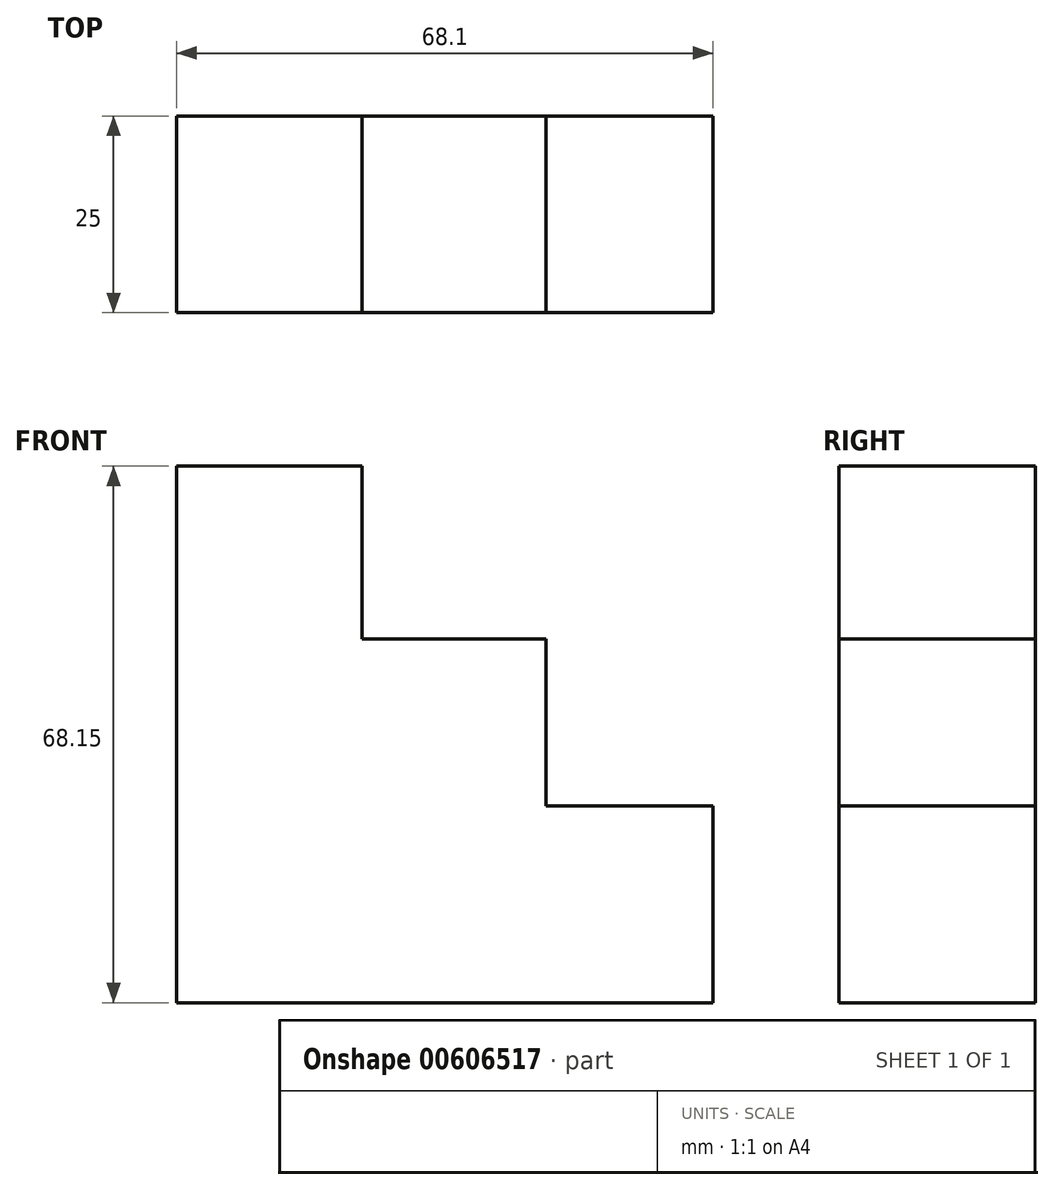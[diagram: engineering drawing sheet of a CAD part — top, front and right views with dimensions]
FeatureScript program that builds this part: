
annotation { "Feature Type Name" : "Feature", "Feature Type Description" : "" }
export const myFeature = defineFeature(function(context is Context, id is Id, definition is map)
    precondition{}
    {
        {
            var Q0;
            Q0=qCreatedBy(makeId("Front.planeOp"),FACE);
            var sketch = newSketch(context, id + "F0", { "sketchPlane" : qUnion([Q0])});
            skLineSegment(sketch, "E0", {"start": v(-51.9, 32.73) * mm, "end": v(-51.9, -35.42) * mm});
            skLineSegment(sketch, "E1", {"start": v(-51.9, -35.42) * mm, "end": v(16.2, -35.42) * mm});
            skLineSegment(sketch, "E2", {"start": v(16.2, -35.42) * mm, "end": v(16.2, -10.42) * mm});
            skLineSegment(sketch, "E3", {"start": v(16.2, -10.42) * mm, "end": v(-4.95, -10.42) * mm});
            skLineSegment(sketch, "E4", {"start": v(-51.9, 32.73) * mm, "end": v(-28.35, 32.73) * mm});
            skLineSegment(sketch, "E5", {"start": v(-4.95, -10.42) * mm, "end": v(-4.95, 10.2) * mm});
            skLineSegment(sketch, "E6", {"start": v(-28.35, 32.73) * mm, "end": v(-28.35, 10.8) * mm});
            skLineSegment(sketch, "E7", {"start": v(-28.35, 10.8) * mm, "end": v(-4.95, 10.8) * mm});
            skLineSegment(sketch, "E8", {"start": v(-4.95, 10.2) * mm, "end": v(-4.95, 10.8) * mm});
            skSolve(sketch);
        }
        {
            var Q0;
            Q0=makeQuery(id+"F0.imprint","IMPRINT",FACE,{"disambiguationData":[TD([[makeQuery(id+"F0.imprint","IMPRINT",EDGE,{"derivedFrom":sQuery(id+"F0.wireOp",EDGE,"E0")}),1.0]])]});
            extrude(context, id + "F1", {"entities" : qUnion([Q0]), "depth" : 25 * mm, "offsetDistance" : 25 * mm});
        }
    });
